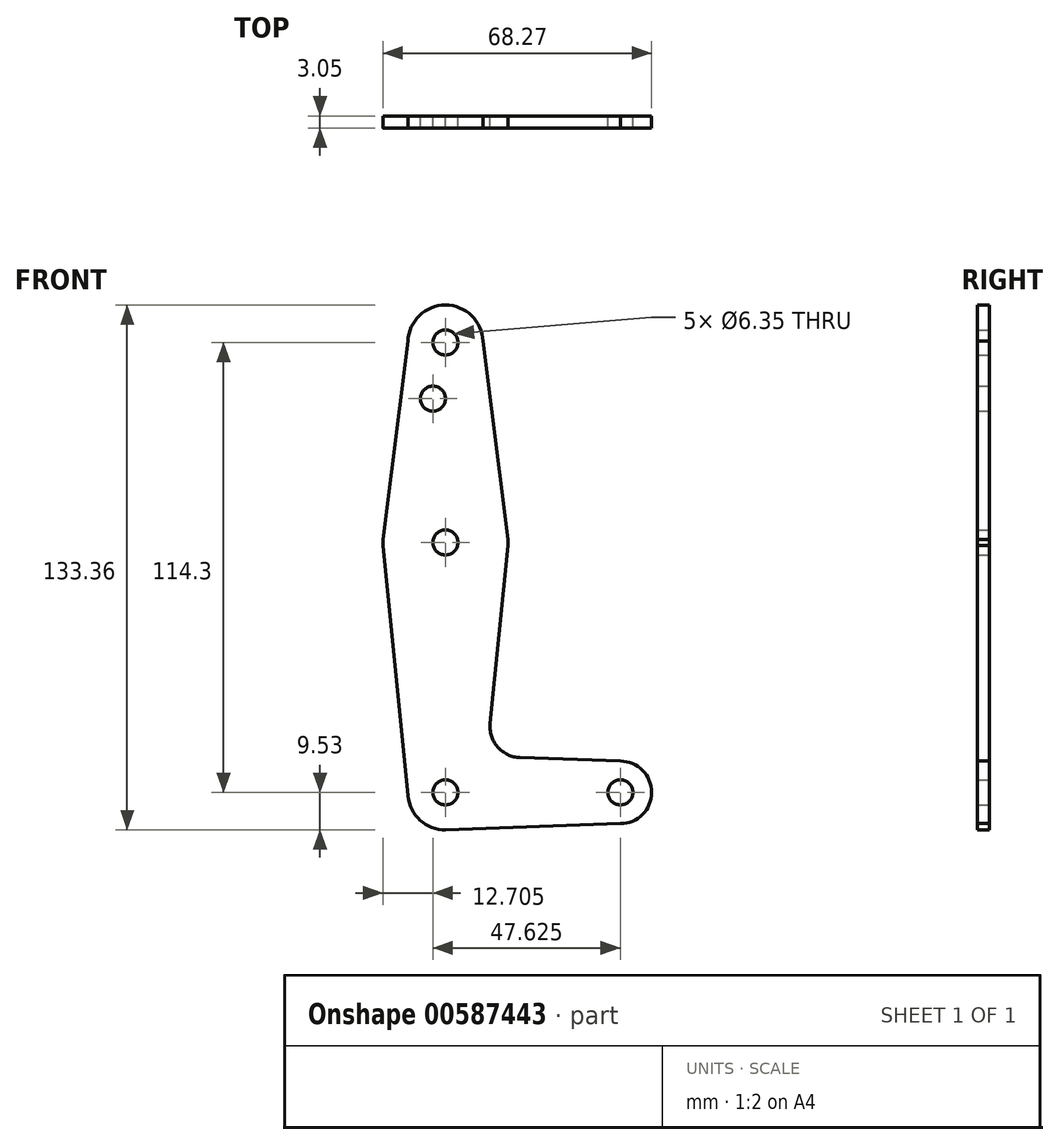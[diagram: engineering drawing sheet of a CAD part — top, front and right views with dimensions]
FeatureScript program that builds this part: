
annotation { "Feature Type Name" : "Feature", "Feature Type Description" : "" }
export const myFeature = defineFeature(function(context is Context, id is Id, definition is map)
    precondition{}
    {
        {
            var Q0;
            Q0=qCreatedBy(makeId("Front.planeOp"),FACE);
            var sketch = newSketch(context, id + "F0", { "sketchPlane" : qUnion([Q0])});
            skLineSegment(sketch, "E0", {"start": v(0, 0) * mm, "end": v(0, 114.3) * mm, "construction": true});
            skLineSegment(sketch, "E1", {"start": v(0, 0) * mm, "end": v(44.45, 0) * mm, "construction": true});
            skCircle(sketch, "E2", {"center": v(0, 114.3) * mm, "radius": 9.53 * mm});
            skCircle(sketch, "E3", {"center": v(0, 63.5) * mm, "radius": 15.88 * mm});
            skCircle(sketch, "E4", {"center": v(0, 0) * mm, "radius": 9.53 * mm});
            skCircle(sketch, "E5", {"center": v(44.45, 0) * mm, "radius": 7.94 * mm});
            skLineSegment(sketch, "E6", {"start": v(-15.86, 64.2) * mm, "end": v(-9.52, 114.64) * mm});
            skLineSegment(sketch, "E7", {"start": v(15.86, 64.2) * mm, "end": v(9.52, 114.64) * mm});
            skLineSegment(sketch, "E8", {"start": v(-15.86, 62.8) * mm, "end": v(-9.48, -0.95) * mm});
            skLineSegment(sketch, "E9", {"start": v(15.86, 62.8) * mm, "end": v(11.33, 17.58) * mm});
            skLineSegment(sketch, "E10", {"start": v(18.96, 8.85) * mm, "end": v(44.45, 7.94) * mm});
            skLineSegment(sketch, "E11", {"start": v(0, -9.52) * mm, "end": v(44.45, -7.94) * mm});
            skCircle(sketch, "E12", {"center": v(0, 114.3) * mm, "radius": 3.18 * mm});
            skCircle(sketch, "E13", {"center": v(-3.18, 100.03) * mm, "radius": 3.18 * mm});
            skCircle(sketch, "E14", {"center": v(0, 63.5) * mm, "radius": 3.18 * mm});
            skCircle(sketch, "E15", {"center": v(0, 0) * mm, "radius": 3.18 * mm});
            skCircle(sketch, "E16", {"center": v(44.45, 0) * mm, "radius": 3.18 * mm});
            skPoint(sketch, "E17.newPointA", {"position": v(9.48, -0.95) * mm});
            skArc(sketch, "E17.filletArc", {"start": v(11.33, 17.58) * mm, "mid": v(13.25, 11.56) * mm, "end": v(18.96, 8.85) * mm});
            skSolve(sketch);
        }
        {
            var Q0;
            Q0=makeQuery(id+"F0.imprint","IMPRINT",FACE,{"disambiguationData":[TD([[makeQuery(id+"F0.imprint","IMPRINT",EDGE,{"derivedFrom":sQuery(id+"F0.wireOp",EDGE,"E12")}),-1.0]])]});
            var Q1;
            Q1=makeQuery(id+"F0.imprint","IMPRINT",FACE,{"disambiguationData":[TD([[makeQuery(id+"F0.imprint","IMPRINT",EDGE,{"derivedFrom":sQuery(id+"F0.wireOp",EDGE,"E13")}),-1.0]])]});
            var Q2;
            Q2=makeQuery(id+"F0.imprint","IMPRINT",FACE,{"disambiguationData":[TD([[makeQuery(id+"F0.imprint","IMPRINT",EDGE,{"derivedFrom":sQuery(id+"F0.wireOp",EDGE,"E14")}),-1.0]])]});
            var Q3;
            {var subQ6=sQuery(id+"F0.wireOp",EDGE,"E10");Q3=makeQuery(id+"F0.imprint","IMPRINT",FACE,{"disambiguationData":[TD([[makeQuery(id+"F0.imprint","IMPRINT",EDGE,{"derivedFrom":subQ6}),-1.0]])]});}
            var Q4;
            Q4=makeQuery(id+"F0.imprint","IMPRINT",FACE,{"disambiguationData":[TD([[makeQuery(id+"F0.imprint","IMPRINT",EDGE,{"derivedFrom":sQuery(id+"F0.wireOp",EDGE,"E15")}),-1.0]])]});
            var Q5;
            Q5=makeQuery(id+"F0.imprint","IMPRINT",FACE,{"disambiguationData":[TD([[makeQuery(id+"F0.imprint","IMPRINT",EDGE,{"derivedFrom":sQuery(id+"F0.wireOp",EDGE,"E16")}),-1.0]])]});
            extrude(context, id + "F1", {"entities" : qUnion([Q0, Q1, Q2, Q3, Q4, Q5]), "depth" : 3.05 * mm, "offsetDistance" : 25.4 * mm});
        }
    });
